# Revit family: 927-00-001-DN80-800
name_source: partatom
category: Pipe Accessories
units: mm (PartAtom-declared; Revit-internal decimal feet)

## family parameters
Always vertical = Yes
Cut with Voids When Loaded = No
Part Type = Valve - Breaks Into
Round Connector Dimension = Use Diameter
Shared = No
Work Plane-Based = No

## types (21) — shared parameters
DN080_PN 10/16 = 927-080-00-020010200
927-080-00-020010200
927-080-00-020010200
927-080-00-020010200
DN100_PN 10/16 = 927-100-00-020010200
927-100-00-020010200
DN150_PN 10/16 = 927-150-00-020010200
DN200_PN10 = 927-200-00-010010200
DN200_PN16 = 927-200-00-020010200
DN250_PN10 = 927-250-00-010010200
DN250_PN16 = 927-250-00-020010200
DN300_PN10 = 927-300-00-010010200
DN300_PN16 = 927-300-00-020010200
DN350_PN10 = 927-350-00-010010200
DN350_PN16 = 927-350-00-020010200
DN400_PN10 = 927-400-00-010010200
DN400_PN16 = 927-400-00-020010200
DN500_PN10 = 927-500-00-010010200
DN500_PN16 = 927-500-00-020010200
DN600_PN10 = 927-600-00-010010200
DN600_PN16 = 927-600-00-020010200
DN700_PN10 = 927-700-00-010010200
DN700_PN16 = 927-700-00-020010200
DN800_PN10 = 927-800-00-010010200
DN800_PN16 = 927-800-00-020010200
Search_table = 927-00-001-DN80-800
URL product pages = https://www.avkvalves.com
zero-valued in all types: 0, Default Elevation, Slot_cut

## per-type parameters (varying)
- DN080_PN 10/16: A=121 mm; B=80 mm; Body_Blend_dim=46 mm; Body_Blend_dim2=80 mm; Body_FL_T=19 mm  [stored 0.062336 ft]; Body_T=6 mm  [stored 0.019685 ft]; Body_arc1=19 mm  [stored 0.062336 ft]; Body_arc_R=180 mm; Body_blend_dim1=72 mm; Body_blend_dim2=80 mm; Body_blend_dim3=80 mm; Body_blend_dim4=60 mm; Body_dim=32 mm  [stored 0.104987 ft]; Body_dim1=48 mm; Body_dim2=56 mm; Body_dim3=22 mm  [stored 0.0721785 ft]; Bolt_dis_H=19 mm  [stored 0.062336 ft]; Bolt_dis_Side=10 mm  [stored 0.0328084 ft]; Bolt_dis_V=23 mm  [stored 0.0754593 ft]; Bolt_location1=20 mm  [stored 0.0656168 ft]; Bolt_location2=20 mm  [stored 0.0656168 ft]; Bolt_location3=54 mm; Bonnet_FL_H1=70 mm; Bonnet_FL_T=19 mm  [stored 0.062336 ft]; Bonnet_FL_dim1=35 mm  [stored 0.114829 ft]; Bonnet_R=20 mm  [stored 0.0656168 ft]; Bonnet_Top_dis=23 mm  [stored 0.0754593 ft]; Bonnet_W=42 mm  [stored 0.137795 ft]; Bonnet_dim=85 mm; Bonnet_dim1=100 mm; Bonnet_dim2=80 mm; Bonnet_dim3=90 mm; Bonnet_sphere_d1=11 mm  [stored 0.0360892 ft]; Bonnet_sphere_d2=60 mm; Bore_R=40 mm  [stored 0.131234 ft]; C=200 mm; D=125 mm; DN=80 mm; Description_=AVK SWING CHECK VALVE, FLANGED; FL_T=16 mm  [stored 0.0524934 ft]; Slot=29 mm  [stored 0.0951444 ft]; Slot_dim1=29 mm  [stored 0.0951444 ft]; Slot_dim2=56 mm; Top_dis_ref=71 mm; Top_rectangle_B=18 mm  [stored 0.0590551 ft]; Top_rectangle_L=42 mm  [stored 0.137795 ft]; rectangle_location=54 mm; top_slot_dis=0 mm  [stored 0 ft]
- DN100_PN 10/16: A=146 mm; B=100 mm; Body_Blend_dim=56 mm; Body_Blend_dim2=100 mm; Body_FL_T=22 mm  [stored 0.0721785 ft]; Body_T=6 mm  [stored 0.019685 ft]; Body_arc1=26 mm; Body_arc_R=230 mm; Body_blend_dim1=88 mm; Body_blend_dim2=96 mm; Body_blend_dim3=88 mm; Body_blend_dim4=66 mm; Body_dim=44 mm  [stored 0.144357 ft]; Body_dim1=58 mm; Body_dim2=72 mm; Body_dim3=31 mm  [stored 0.101706 ft]; Bolt_dis_H=22 mm  [stored 0.0721785 ft]; Bolt_dis_Side=11 mm  [stored 0.0360892 ft]; Bolt_dis_V=26 mm; Bolt_location1=19 mm  [stored 0.062336 ft]; Bolt_location2=22 mm  [stored 0.0721785 ft]; Bolt_location3=65 mm; Bonnet_FL_H1=77 mm; Bonnet_FL_T=26 mm; Bonnet_FL_dim1=30 mm  [stored 0.0984252 ft]; Bonnet_R=20 mm  [stored 0.0656168 ft]; Bonnet_Top_dis=29 mm  [stored 0.0951444 ft]; Bonnet_W=51 mm; Bonnet_dim=100 mm; Bonnet_dim1=110 mm; Bonnet_dim2=88 mm; Bonnet_dim3=105 mm; Bonnet_sphere_d1=13 mm  [stored 0.0426509 ft]; Bonnet_sphere_d2=72 mm; Bore_R=50 mm; C=220 mm; D=140 mm; DN=100 mm; Description_=AVK SWING CHECK VALVE, FLANGED; FL_T=22 mm  [stored 0.0721785 ft]; Slot=35 mm  [stored 0.114829 ft]; Slot_dim1=33 mm  [stored 0.108268 ft]; Slot_dim2=72 mm; Top_dis_ref=86 mm; Top_rectangle_B=22 mm  [stored 0.0721785 ft]; Top_rectangle_L=51 mm; rectangle_location=65 mm; top_slot_dis=0 mm  [stored 0 ft]
- DN150_PN 10/16: A=178 mm; B=150 mm; Body_Blend_dim=81 mm; Body_Blend_dim2=150 mm; Body_FL_T=25 mm  [stored 0.082021 ft]; Body_T=6 mm  [stored 0.019685 ft]; Body_arc1=30 mm  [stored 0.0984252 ft]; Body_arc_R=280 mm; Body_blend_dim1=107 mm; Body_blend_dim2=117 mm; Body_blend_dim3=114 mm; Body_blend_dim4=86 mm; Body_dim=50 mm; Body_dim1=71 mm; Body_dim2=100 mm; Body_dim3=35 mm  [stored 0.114829 ft]; Bolt_dis_H=25 mm  [stored 0.082021 ft]; Bolt_dis_Side=13 mm  [stored 0.0426509 ft]; Bolt_dis_V=30 mm  [stored 0.0984252 ft]; Bolt_location1=27 mm  [stored 0.0885827 ft]; Bolt_location2=28 mm  [stored 0.0918635 ft]; Bolt_location3=79 mm; Bonnet_FL_H1=100 mm; Bonnet_FL_T=30 mm  [stored 0.0984252 ft]; Bonnet_FL_dim1=34 mm  [stored 0.111549 ft]; Bonnet_R=15 mm  [stored 0.0492126 ft]; Bonnet_Top_dis=35 mm  [stored 0.114829 ft]; Bonnet_W=62 mm; Bonnet_dim=125 mm; Bonnet_dim1=143 mm; Bonnet_dim2=114 mm; Bonnet_dim3=130 mm; Bonnet_sphere_d1=15 mm  [stored 0.0492126 ft]; Bonnet_sphere_d2=88 mm; Bore_R=75 mm; C=285 mm; D=175 mm; DN=150 mm; Description_=AVK SWING CHECK VALVE, FLANGED; FL_T=25 mm  [stored 0.082021 ft]; Slot=43 mm  [stored 0.141076 ft]; Slot_dim1=38 mm; Slot_dim2=100 mm; Top_dis_ref=105 mm; Top_rectangle_B=26 mm; Top_rectangle_L=62 mm; rectangle_location=79 mm; top_slot_dis=0 mm  [stored 0 ft]
- DN200_PN10: A=248 mm; B=200 mm; Body_Blend_dim=106 mm; Body_Blend_dim2=200 mm; Body_FL_T=27 mm  [stored 0.0885827 ft]; Body_T=6 mm  [stored 0.019685 ft]; Body_arc1=34 mm  [stored 0.111549 ft]; Body_arc_R=430 mm; Body_blend_dim1=149 mm; Body_blend_dim2=163 mm; Body_blend_dim3=136 mm; Body_blend_dim4=102 mm; Body_dim=56 mm; Body_dim1=99 mm; Body_dim2=128 mm; Body_dim3=39 mm  [stored 0.127953 ft]; Bolt_dis_H=27 mm  [stored 0.0885827 ft]; Bolt_dis_Side=14 mm  [stored 0.0459318 ft]; Bolt_dis_V=32 mm  [stored 0.104987 ft]; Bolt_location1=24 mm  [stored 0.0787402 ft]; Bolt_location2=35 mm  [stored 0.114829 ft]; Bolt_location3=110 mm; Bonnet_FL_H1=119 mm; Bonnet_FL_T=34 mm  [stored 0.111549 ft]; Bonnet_FL_dim1=34 mm  [stored 0.111549 ft]; Bonnet_R=18 mm  [stored 0.0590551 ft]; Bonnet_Top_dis=54 mm; Bonnet_W=87 mm; Bonnet_dim=170 mm; Bonnet_dim1=170 mm; Bonnet_dim2=136 mm; Bonnet_dim3=175 mm; Bonnet_sphere_d1=16 mm  [stored 0.0524934 ft]; Bonnet_sphere_d2=123 mm; Bore_R=100 mm; C=340 mm; D=215 mm; DN=200 mm; Description_=AVK SWING CHECK VALVE, FLANGED; FL_T=28 mm  [stored 0.0918635 ft]; Slot=60 mm; Slot_dim1=41 mm  [stored 0.134514 ft]; Slot_dim2=128 mm; Top_dis_ref=146 mm; Top_rectangle_B=37 mm  [stored 0.121391 ft]; Top_rectangle_L=86 mm; rectangle_location=110 mm; top_slot_dis=0 mm  [stored 0 ft]
- DN200_PN16: A=248 mm; B=200 mm; Body_Blend_dim=106 mm; Body_Blend_dim2=200 mm; Body_FL_T=27 mm  [stored 0.0885827 ft]; Body_T=6 mm  [stored 0.019685 ft]; Body_arc1=34 mm  [stored 0.111549 ft]; Body_arc_R=430 mm; Body_blend_dim1=149 mm; Body_blend_dim2=163 mm; Body_blend_dim3=136 mm; Body_blend_dim4=102 mm; Body_dim=56 mm; Body_dim1=99 mm; Body_dim2=128 mm; Body_dim3=39 mm  [stored 0.127953 ft]; Bolt_dis_H=27 mm  [stored 0.0885827 ft]; Bolt_dis_Side=14 mm  [stored 0.0459318 ft]; Bolt_dis_V=32 mm  [stored 0.104987 ft]; Bolt_location1=24 mm  [stored 0.0787402 ft]; Bolt_location2=35 mm  [stored 0.114829 ft]; Bolt_location3=110 mm; Bonnet_FL_H1=119 mm; Bonnet_FL_T=34 mm  [stored 0.111549 ft]; Bonnet_FL_dim1=34 mm  [stored 0.111549 ft]; Bonnet_R=21 mm  [stored 0.0688976 ft]; Bonnet_Top_dis=54 mm; Bonnet_W=87 mm; Bonnet_dim=170 mm; Bonnet_dim1=170 mm; Bonnet_dim2=136 mm; Bonnet_dim3=175 mm; Bonnet_sphere_d1=16 mm  [stored 0.0524934 ft]; Bonnet_sphere_d2=123 mm; Bore_R=100 mm; C=340 mm; D=215 mm; DN=200 mm; Description_=AVK SWING CHECK VALVE, FLANGED; FL_T=28 mm  [stored 0.0918635 ft]; Slot=60 mm; Slot_dim1=41 mm  [stored 0.134514 ft]; Slot_dim2=128 mm; Top_dis_ref=146 mm; Top_rectangle_B=37 mm  [stored 0.121391 ft]; Top_rectangle_L=86 mm; rectangle_location=110 mm; top_slot_dis=0 mm  [stored 0 ft]
- DN250_PN10: A=311 mm; B=250 mm; Body_Blend_dim=132 mm; Body_Blend_dim2=250 mm; Body_FL_T=31 mm  [stored 0.101706 ft]; Body_T=7 mm  [stored 0.0229659 ft]; Body_arc1=35 mm  [stored 0.114829 ft]; Body_arc_R=545 mm; Body_blend_dim1=187 mm; Body_blend_dim2=205 mm; Body_blend_dim3=160 mm; Body_blend_dim4=120 mm; Body_dim=58 mm; Body_dim1=124 mm; Body_dim2=154 mm; Body_dim3=41 mm  [stored 0.134514 ft]; Bolt_dis_H=31 mm  [stored 0.101706 ft]; Bolt_dis_Side=16 mm  [stored 0.0524934 ft]; Bolt_dis_V=37 mm  [stored 0.121391 ft]; Bolt_location1=23 mm  [stored 0.0754593 ft]; Bolt_location2=54 mm; Bolt_location3=139 mm; Bonnet_FL_H1=140 mm; Bonnet_FL_T=35 mm  [stored 0.114829 ft]; Bonnet_FL_dim1=37 mm  [stored 0.121391 ft]; Bonnet_R=24 mm  [stored 0.0787402 ft]; Bonnet_Top_dis=68 mm; Bonnet_W=109 mm; Bonnet_dim=230 mm; Bonnet_dim1=200 mm; Bonnet_dim2=160 mm; Bonnet_dim3=235 mm; Bonnet_sphere_d1=18 mm  [stored 0.0590551 ft]; Bonnet_sphere_d2=154 mm; Bore_R=125 mm; C=400 mm; D=280 mm; DN=250 mm; Description_=AVK SWING CHECK VALVE, FLANGED; FL_T=29 mm  [stored 0.0951444 ft]; Slot=75 mm; Slot_dim1=47 mm; Slot_dim2=154 mm; Top_dis_ref=183 mm; Top_rectangle_B=46 mm; Top_rectangle_L=108 mm; rectangle_location=139 mm; top_slot_dis=0 mm  [stored 0 ft]
- DN250_PN16: A=311 mm; B=250 mm; Body_Blend_dim=132 mm; Body_Blend_dim2=250 mm; Body_FL_T=31 mm  [stored 0.101706 ft]; Body_T=7 mm  [stored 0.0229659 ft]; Body_arc1=35 mm  [stored 0.114829 ft]; Body_arc_R=545 mm; Body_blend_dim1=187 mm; Body_blend_dim2=205 mm; Body_blend_dim3=160 mm; Body_blend_dim4=120 mm; Body_dim=58 mm; Body_dim1=124 mm; Body_dim2=154 mm; Body_dim3=41 mm  [stored 0.134514 ft]; Bolt_dis_H=31 mm  [stored 0.101706 ft]; Bolt_dis_Side=16 mm  [stored 0.0524934 ft]; Bolt_dis_V=37 mm  [stored 0.121391 ft]; Bolt_location1=23 mm  [stored 0.0754593 ft]; Bolt_location2=54 mm; Bolt_location3=139 mm; Bonnet_FL_H1=140 mm; Bonnet_FL_T=35 mm  [stored 0.114829 ft]; Bonnet_FL_dim1=37 mm  [stored 0.121391 ft]; Bonnet_R=24 mm  [stored 0.0787402 ft]; Bonnet_Top_dis=68 mm; Bonnet_W=109 mm; Bonnet_dim=230 mm; Bonnet_dim1=200 mm; Bonnet_dim2=160 mm; Bonnet_dim3=235 mm; Bonnet_sphere_d1=18 mm  [stored 0.0590551 ft]; Bonnet_sphere_d2=154 mm; Bore_R=125 mm; C=400 mm; D=280 mm; DN=250 mm; Description_=AVK SWING CHECK VALVE, FLANGED; FL_T=29 mm  [stored 0.0951444 ft]; Slot=75 mm; Slot_dim1=47 mm; Slot_dim2=154 mm; Top_dis_ref=183 mm; Top_rectangle_B=46 mm; Top_rectangle_L=108 mm; rectangle_location=139 mm; top_slot_dis=0 mm  [stored 0 ft]
- DN300_PN10: A=349 mm; B=300 mm; Body_Blend_dim=157 mm; Body_Blend_dim2=300 mm; Body_FL_T=34 mm  [stored 0.111549 ft]; Body_T=7 mm  [stored 0.0229659 ft]; Body_arc1=37 mm  [stored 0.121391 ft]; Body_arc_R=590 mm; Body_blend_dim1=209 mm; Body_blend_dim2=230 mm; Body_blend_dim3=182 mm; Body_blend_dim4=137 mm; Body_dim=62 mm; Body_dim1=140 mm; Body_dim2=181 mm; Body_dim3=43 mm  [stored 0.141076 ft]; Bolt_dis_H=34 mm  [stored 0.111549 ft]; Bolt_dis_Side=17 mm; Bolt_dis_V=41 mm  [stored 0.134514 ft]; Bolt_location1=27 mm  [stored 0.0885827 ft]; Bolt_location2=55 mm; Bolt_location3=155 mm; Bonnet_FL_H1=159 mm; Bonnet_FL_T=37 mm  [stored 0.121391 ft]; Bonnet_FL_dim1=37 mm  [stored 0.121391 ft]; Bonnet_R=27 mm  [stored 0.0885827 ft]; Bonnet_Top_dis=74 mm; Bonnet_W=122 mm; Bonnet_dim=250 mm; Bonnet_dim1=228 mm; Bonnet_dim2=182 mm; Bonnet_dim3=255 mm; Bonnet_sphere_d1=20 mm  [stored 0.0656168 ft]; Bonnet_sphere_d2=173 mm; Bore_R=150 mm; C=455 mm; D=300 mm; DN=300 mm; Description_=AVK SWING CHECK VALVE, FLANGED; FL_T=31 mm  [stored 0.101706 ft]; Slot=85 mm; Slot_dim1=51 mm; Slot_dim2=181 mm; Top_dis_ref=206 mm; Top_rectangle_B=52 mm; Top_rectangle_L=121 mm; rectangle_location=155 mm; top_slot_dis=0 mm  [stored 0 ft]
- DN300_PN16: A=349 mm; B=300 mm; Body_Blend_dim=157 mm; Body_Blend_dim2=300 mm; Body_FL_T=34 mm  [stored 0.111549 ft]; Body_T=7 mm  [stored 0.0229659 ft]; Body_arc1=37 mm  [stored 0.121391 ft]; Body_arc_R=590 mm; Body_blend_dim1=209 mm; Body_blend_dim2=230 mm; Body_blend_dim3=182 mm; Body_blend_dim4=137 mm; Body_dim=62 mm; Body_dim1=140 mm; Body_dim2=181 mm; Body_dim3=43 mm  [stored 0.141076 ft]; Bolt_dis_H=34 mm  [stored 0.111549 ft]; Bolt_dis_Side=17 mm; Bolt_dis_V=41 mm  [stored 0.134514 ft]; Bolt_location1=27 mm  [stored 0.0885827 ft]; Bolt_location2=55 mm; Bolt_location3=155 mm; Bonnet_FL_H1=159 mm; Bonnet_FL_T=37 mm  [stored 0.121391 ft]; Bonnet_FL_dim1=37 mm  [stored 0.121391 ft]; Bonnet_R=27 mm  [stored 0.0885827 ft]; Bonnet_Top_dis=74 mm; Bonnet_W=122 mm; Bonnet_dim=250 mm; Bonnet_dim1=228 mm; Bonnet_dim2=182 mm; Bonnet_dim3=255 mm; Bonnet_sphere_d1=20 mm  [stored 0.0656168 ft]; Bonnet_sphere_d2=173 mm; Bore_R=150 mm; C=455 mm; D=300 mm; DN=300 mm; Description_=AVK SWING CHECK VALVE, FLANGED; FL_T=31 mm  [stored 0.101706 ft]; Slot=85 mm; Slot_dim1=51 mm; Slot_dim2=181 mm; Top_dis_ref=206 mm; Top_rectangle_B=52 mm; Top_rectangle_L=121 mm; rectangle_location=155 mm; top_slot_dis=0 mm  [stored 0 ft]
- DN350_PN10: A=394 mm; B=350 mm; Body_Blend_dim=183 mm; Body_Blend_dim2=350 mm; Body_FL_T=37 mm  [stored 0.121391 ft]; Body_T=8 mm  [stored 0.0262467 ft]; Body_arc1=40 mm  [stored 0.131234 ft]; Body_arc_R=670 mm; Body_blend_dim1=236 mm; Body_blend_dim2=260 mm; Body_blend_dim3=202 mm; Body_blend_dim4=152 mm; Body_dim=66 mm; Body_dim1=157 mm; Body_dim2=208 mm; Body_dim3=46 mm; Bolt_dis_H=37 mm  [stored 0.121391 ft]; Bolt_dis_Side=19 mm  [stored 0.062336 ft]; Bolt_dis_V=44 mm  [stored 0.144357 ft]; Bolt_location1=29 mm  [stored 0.0951444 ft]; Bolt_location2=73 mm; Bolt_location3=175 mm; Bonnet_FL_H1=177 mm; Bonnet_FL_T=40 mm  [stored 0.131234 ft]; Bonnet_FL_dim1=36 mm  [stored 0.11811 ft]; Bonnet_R=30 mm  [stored 0.0984252 ft]; Bonnet_Top_dis=84 mm; Bonnet_W=138 mm; Bonnet_dim=300 mm; Bonnet_dim1=253 mm; Bonnet_dim2=202 mm; Bonnet_dim3=305 mm; Bonnet_sphere_d1=22 mm  [stored 0.0721785 ft]; Bonnet_sphere_d2=195 mm; Bore_R=175 mm; C=505 mm; D=315 mm; DN=350 mm; Description_=AVK SWING CHECK VALVE, FLANGED; FL_T=33 mm  [stored 0.108268 ft]; Slot=95 mm; Slot_dim1=56 mm; Slot_dim2=208 mm; Top_dis_ref=232 mm; Top_rectangle_B=58 mm; Top_rectangle_L=136 mm; rectangle_location=175 mm; top_slot_dis=0 mm  [stored 0 ft]
- DN350_PN16: A=394 mm; B=350 mm; Body_Blend_dim=183 mm; Body_Blend_dim2=350 mm; Body_FL_T=37 mm  [stored 0.121391 ft]; Body_T=8 mm  [stored 0.0262467 ft]; Body_arc1=40 mm  [stored 0.131234 ft]; Body_arc_R=670 mm; Body_blend_dim1=236 mm; Body_blend_dim2=260 mm; Body_blend_dim3=202 mm; Body_blend_dim4=152 mm; Body_dim=66 mm; Body_dim1=157 mm; Body_dim2=208 mm; Body_dim3=46 mm; Bolt_dis_H=37 mm  [stored 0.121391 ft]; Bolt_dis_Side=19 mm  [stored 0.062336 ft]; Bolt_dis_V=44 mm  [stored 0.144357 ft]; Bolt_location1=29 mm  [stored 0.0951444 ft]; Bolt_location2=73 mm; Bolt_location3=175 mm; Bonnet_FL_H1=177 mm; Bonnet_FL_T=40 mm  [stored 0.131234 ft]; Bonnet_FL_dim1=36 mm  [stored 0.11811 ft]; Bonnet_R=30 mm  [stored 0.0984252 ft]; Bonnet_Top_dis=84 mm; Bonnet_W=138 mm; Bonnet_dim=300 mm; Bonnet_dim1=253 mm; Bonnet_dim2=202 mm; Bonnet_dim3=305 mm; Bonnet_sphere_d1=22 mm  [stored 0.0721785 ft]; Bonnet_sphere_d2=195 mm; Bore_R=175 mm; C=505 mm; D=315 mm; DN=350 mm; Description_=AVK SWING CHECK VALVE, FLANGED; FL_T=33 mm  [stored 0.108268 ft]; Slot=95 mm; Slot_dim1=56 mm; Slot_dim2=208 mm; Top_dis_ref=232 mm; Top_rectangle_B=58 mm; Top_rectangle_L=136 mm; rectangle_location=175 mm; top_slot_dis=0 mm  [stored 0 ft]
- DN400_PN10: A=457 mm; B=400 mm; Body_Blend_dim=208 mm; Body_Blend_dim2=400 mm; Body_FL_T=39 mm  [stored 0.127953 ft]; Body_T=8 mm  [stored 0.0262467 ft]; Body_arc1=42 mm  [stored 0.137795 ft]; Body_arc_R=770 mm; Body_blend_dim1=274 mm; Body_blend_dim2=302 mm; Body_blend_dim3=232 mm; Body_blend_dim4=174 mm; Body_dim=70 mm; Body_dim1=183 mm; Body_dim2=235 mm; Body_dim3=49 mm; Bolt_dis_H=39 mm  [stored 0.127953 ft]; Bolt_dis_Side=20 mm  [stored 0.0656168 ft]; Bolt_dis_V=47 mm; Bolt_location1=32 mm  [stored 0.104987 ft]; Bolt_location2=79 mm; Bolt_location3=204 mm; Bonnet_FL_H1=203 mm; Bonnet_FL_T=42 mm  [stored 0.137795 ft]; Bonnet_FL_dim1=44 mm  [stored 0.144357 ft]; Bonnet_R=33 mm  [stored 0.108268 ft]; Bonnet_Top_dis=96 mm; Bonnet_W=160 mm; Bonnet_dim=340 mm; Bonnet_dim1=290 mm; Bonnet_dim2=232 mm; Bonnet_dim3=345 mm; Bonnet_sphere_d1=23 mm  [stored 0.0754593 ft]; Bonnet_sphere_d2=226 mm; Bore_R=200 mm; C=580 mm; D=355 mm; DN=400 mm; Description_=AVK SWING CHECK VALVE, FLANGED; FL_T=35 mm  [stored 0.114829 ft]; Slot=111 mm; Slot_dim1=59 mm; Slot_dim2=235 mm; Top_dis_ref=269 mm; Top_rectangle_B=68 mm; Top_rectangle_L=158 mm; rectangle_location=204 mm; top_slot_dis=0 mm  [stored 0 ft]
- DN400_PN16: A=457 mm; B=400 mm; Body_Blend_dim=208 mm; Body_Blend_dim2=400 mm; Body_FL_T=39 mm  [stored 0.127953 ft]; Body_T=8 mm  [stored 0.0262467 ft]; Body_arc1=42 mm  [stored 0.137795 ft]; Body_arc_R=770 mm; Body_blend_dim1=274 mm; Body_blend_dim2=302 mm; Body_blend_dim3=232 mm; Body_blend_dim4=174 mm; Body_dim=70 mm; Body_dim1=183 mm; Body_dim2=235 mm; Body_dim3=49 mm; Bolt_dis_H=39 mm  [stored 0.127953 ft]; Bolt_dis_Side=20 mm  [stored 0.0656168 ft]; Bolt_dis_V=47 mm; Bolt_location1=32 mm  [stored 0.104987 ft]; Bolt_location2=79 mm; Bolt_location3=204 mm; Bonnet_FL_H1=203 mm; Bonnet_FL_T=42 mm  [stored 0.137795 ft]; Bonnet_FL_dim1=44 mm  [stored 0.144357 ft]; Bonnet_R=33 mm  [stored 0.108268 ft]; Bonnet_Top_dis=96 mm; Bonnet_W=160 mm; Bonnet_dim=340 mm; Bonnet_dim1=290 mm; Bonnet_dim2=232 mm; Bonnet_dim3=345 mm; Bonnet_sphere_d1=23 mm  [stored 0.0754593 ft]; Bonnet_sphere_d2=226 mm; Bore_R=200 mm; C=580 mm; D=355 mm; DN=400 mm; Description_=AVK SWING CHECK VALVE, FLANGED; FL_T=35 mm  [stored 0.114829 ft]; Slot=111 mm; Slot_dim1=59 mm; Slot_dim2=235 mm; Top_dis_ref=269 mm; Top_rectangle_B=68 mm; Top_rectangle_L=158 mm; rectangle_location=204 mm; top_slot_dis=0 mm  [stored 0 ft]
- DN500_PN10: A=508 mm; B=500 mm; Body_Blend_dim=259 mm; Body_Blend_dim2=500 mm; Body_FL_T=43 mm  [stored 0.141076 ft]; Body_T=9 mm  [stored 0.0295276 ft]; Body_arc1=44 mm  [stored 0.144357 ft]; Body_arc_R=890 mm; Body_blend_dim1=305 mm; Body_blend_dim2=335 mm; Body_blend_dim3=279 mm; Body_blend_dim4=209 mm; Body_dim=74 mm; Body_dim1=203 mm; Body_dim2=287 mm; Body_dim3=52 mm; Bolt_dis_H=43 mm  [stored 0.141076 ft]; Bolt_dis_Side=22 mm  [stored 0.0721785 ft]; Bolt_dis_V=52 mm; Bolt_location1=49 mm; Bolt_location2=109 mm; Bolt_location3=226 mm; Bonnet_FL_H1=244 mm; Bonnet_FL_T=44 mm  [stored 0.144357 ft]; Bonnet_FL_dim1=50 mm; Bonnet_R=36 mm  [stored 0.11811 ft]; Bonnet_Top_dis=111 mm; Bonnet_W=178 mm; Bonnet_dim=410 mm; Bonnet_dim1=349 mm; Bonnet_dim2=279 mm; Bonnet_dim3=415 mm; Bonnet_sphere_d1=25 mm  [stored 0.082021 ft]; Bonnet_sphere_d2=251 mm; Bore_R=250 mm; C=698 mm; D=430 mm; DN=500 mm; Description_=AVK SWING CHECK VALVE, FLANGED; FL_T=37 mm  [stored 0.121391 ft]; Slot=123 mm; Slot_dim1=65 mm; Slot_dim2=287 mm; Top_dis_ref=299 mm; Top_rectangle_B=75 mm; Top_rectangle_L=176 mm; rectangle_location=226 mm; top_slot_dis=0 mm  [stored 0 ft]
- DN500_PN16: A=508 mm; B=500 mm; Body_Blend_dim=259 mm; Body_Blend_dim2=500 mm; Body_FL_T=43 mm  [stored 0.141076 ft]; Body_T=9 mm  [stored 0.0295276 ft]; Body_arc1=44 mm  [stored 0.144357 ft]; Body_arc_R=890 mm; Body_blend_dim1=305 mm; Body_blend_dim2=335 mm; Body_blend_dim3=279 mm; Body_blend_dim4=209 mm; Body_dim=74 mm; Body_dim1=203 mm; Body_dim2=287 mm; Body_dim3=52 mm; Bolt_dis_H=43 mm  [stored 0.141076 ft]; Bolt_dis_Side=22 mm  [stored 0.0721785 ft]; Bolt_dis_V=52 mm; Bolt_location1=49 mm; Bolt_location2=109 mm; Bolt_location3=226 mm; Bonnet_FL_H1=244 mm; Bonnet_FL_T=44 mm  [stored 0.144357 ft]; Bonnet_FL_dim1=50 mm; Bonnet_R=36 mm  [stored 0.11811 ft]; Bonnet_Top_dis=111 mm; Bonnet_W=178 mm; Bonnet_dim=410 mm; Bonnet_dim1=349 mm; Bonnet_dim2=279 mm; Bonnet_dim3=415 mm; Bonnet_sphere_d1=25 mm  [stored 0.082021 ft]; Bonnet_sphere_d2=251 mm; Bore_R=250 mm; C=698 mm; D=430 mm; DN=500 mm; Description_=AVK SWING CHECK VALVE, FLANGED; FL_T=37 mm  [stored 0.121391 ft]; Slot=123 mm; Slot_dim1=65 mm; Slot_dim2=287 mm; Top_dis_ref=299 mm; Top_rectangle_B=75 mm; Top_rectangle_L=176 mm; rectangle_location=226 mm; top_slot_dis=0 mm  [stored 0 ft]
- DN600_PN10: A=610 mm; B=600 mm; Body_Blend_dim=309 mm; Body_Blend_dim2=600 mm; Body_FL_T=46 mm; Body_T=9 mm  [stored 0.0295276 ft]; Body_arc1=47 mm; Body_arc_R=1000 mm; Body_blend_dim1=366 mm; Body_blend_dim2=402 mm; Body_blend_dim3=312 mm; Body_blend_dim4=234 mm; Body_dim=78 mm; Body_dim1=244 mm; Body_dim2=339 mm; Body_dim3=55 mm; Bolt_dis_H=46 mm; Bolt_dis_Side=23 mm  [stored 0.0754593 ft]; Bolt_dis_V=55 mm; Bolt_location1=44 mm  [stored 0.144357 ft]; Bolt_location2=116 mm; Bolt_location3=272 mm; Bonnet_FL_H1=273 mm; Bonnet_FL_T=47 mm; Bonnet_FL_dim1=41 mm  [stored 0.134514 ft]; Bonnet_R=39 mm  [stored 0.127953 ft]; Bonnet_Top_dis=125 mm; Bonnet_W=213 mm; Bonnet_dim=470 mm; Bonnet_dim1=390 mm; Bonnet_dim2=312 mm; Bonnet_dim3=475 mm; Bonnet_sphere_d1=27 mm  [stored 0.0885827 ft]; Bonnet_sphere_d2=302 mm; Bore_R=300 mm; C=780 mm; D=495 mm; DN=600 mm; Description_=AVK SWING CHECK VALVE, FLANGED; FL_T=39 mm  [stored 0.127953 ft]; Slot=148 mm; Slot_dim1=69 mm; Slot_dim2=339 mm; Top_dis_ref=359 mm; Top_rectangle_B=91 mm; Top_rectangle_L=211 mm; rectangle_location=272 mm; top_slot_dis=0 mm  [stored 0 ft]
- DN600_PN16: A=610 mm; B=600 mm; Body_Blend_dim=309 mm; Body_Blend_dim2=600 mm; Body_FL_T=46 mm; Body_T=9 mm  [stored 0.0295276 ft]; Body_arc1=47 mm; Body_arc_R=1000 mm; Body_blend_dim1=366 mm; Body_blend_dim2=402 mm; Body_blend_dim3=312 mm; Body_blend_dim4=234 mm; Body_dim=78 mm; Body_dim1=244 mm; Body_dim2=339 mm; Body_dim3=55 mm; Bolt_dis_H=46 mm; Bolt_dis_Side=23 mm  [stored 0.0754593 ft]; Bolt_dis_V=55 mm; Bolt_location1=44 mm  [stored 0.144357 ft]; Bolt_location2=116 mm; Bolt_location3=272 mm; Bonnet_FL_H1=273 mm; Bonnet_FL_T=47 mm; Bonnet_FL_dim1=41 mm  [stored 0.134514 ft]; Bonnet_R=39 mm  [stored 0.127953 ft]; Bonnet_Top_dis=125 mm; Bonnet_W=213 mm; Bonnet_dim=470 mm; Bonnet_dim1=390 mm; Bonnet_dim2=312 mm; Bonnet_dim3=475 mm; Bonnet_sphere_d1=27 mm  [stored 0.0885827 ft]; Bonnet_sphere_d2=302 mm; Bore_R=300 mm; C=780 mm; D=495 mm; DN=600 mm; Description_=AVK SWING CHECK VALVE, FLANGED; FL_T=39 mm  [stored 0.127953 ft]; Slot=148 mm; Slot_dim1=69 mm; Slot_dim2=339 mm; Top_dis_ref=359 mm; Top_rectangle_B=91 mm; Top_rectangle_L=211 mm; rectangle_location=272 mm; top_slot_dis=0 mm  [stored 0 ft]
- DN700_PN10: A=750 mm; B=700 mm; Body_Blend_dim=360 mm; Body_Blend_dim2=700 mm; Body_FL_T=49 mm; Body_T=10 mm  [stored 0.0328084 ft]; Body_arc1=49 mm; Body_arc_R=1220 mm; Body_blend_dim1=450 mm; Body_blend_dim2=495 mm; Body_blend_dim3=364 mm; Body_blend_dim4=273 mm; Body_dim=82 mm; Body_dim1=300 mm; Body_dim2=391 mm; Body_dim3=57 mm; Bolt_dis_H=49 mm; Bolt_dis_Side=25 mm  [stored 0.082021 ft]; Bolt_dis_V=59 mm; Bolt_location1=42 mm  [stored 0.137795 ft]; Bolt_location2=143 mm; Bolt_location3=334 mm; Bonnet_FL_H1=319 mm; Bonnet_FL_T=49 mm; Bonnet_FL_dim1=51 mm; Bonnet_R=42 mm  [stored 0.137795 ft]; Bonnet_Top_dis=153 mm; Bonnet_W=263 mm; Bonnet_dim=580 mm; Bonnet_dim1=455 mm; Bonnet_dim2=364 mm; Bonnet_dim3=585 mm; Bonnet_sphere_d1=29 mm  [stored 0.0951444 ft]; Bonnet_sphere_d2=371 mm; Bore_R=350 mm; C=910 mm; D=580 mm; DN=700 mm; Description_=AVK SWING CHECK VALVE, FLANGED; FL_T=41 mm  [stored 0.134514 ft]; Slot=182 mm; Slot_dim1=74 mm; Slot_dim2=391 mm; Top_dis_ref=442 mm; Top_rectangle_B=111 mm; Top_rectangle_L=260 mm; rectangle_location=334 mm; top_slot_dis=0 mm  [stored 0 ft]
- DN700_PN16: A=750 mm; B=700 mm; Body_Blend_dim=360 mm; Body_Blend_dim2=700 mm; Body_FL_T=49 mm; Body_T=10 mm  [stored 0.0328084 ft]; Body_arc1=49 mm; Body_arc_R=1220 mm; Body_blend_dim1=450 mm; Body_blend_dim2=495 mm; Body_blend_dim3=364 mm; Body_blend_dim4=273 mm; Body_dim=82 mm; Body_dim1=300 mm; Body_dim2=391 mm; Body_dim3=57 mm; Bolt_dis_H=49 mm; Bolt_dis_Side=25 mm  [stored 0.082021 ft]; Bolt_dis_V=59 mm; Bolt_location1=42 mm  [stored 0.137795 ft]; Bolt_location2=143 mm; Bolt_location3=334 mm; Bonnet_FL_H1=319 mm; Bonnet_FL_T=49 mm; Bonnet_FL_dim1=51 mm; Bonnet_R=42 mm  [stored 0.137795 ft]; Bonnet_Top_dis=153 mm; Bonnet_W=263 mm; Bonnet_dim=580 mm; Bonnet_dim1=455 mm; Bonnet_dim2=364 mm; Bonnet_dim3=585 mm; Bonnet_sphere_d1=29 mm  [stored 0.0951444 ft]; Bonnet_sphere_d2=371 mm; Bore_R=350 mm; C=910 mm; D=580 mm; DN=700 mm; Description_=AVK SWING CHECK VALVE, FLANGED; FL_T=41 mm  [stored 0.134514 ft]; Slot=182 mm; Slot_dim1=74 mm; Slot_dim2=391 mm; Top_dis_ref=442 mm; Top_rectangle_B=111 mm; Top_rectangle_L=260 mm; rectangle_location=334 mm; top_slot_dis=0 mm  [stored 0 ft]
- DN800_PN10: A=850 mm; B=780 mm; Body_Blend_dim=410 mm; Body_Blend_dim2=800 mm; Body_FL_T=51 mm; Body_T=10 mm  [stored 0.0328084 ft]; Body_arc1=52 mm; Body_arc_R=1500 mm; Body_blend_dim1=510 mm; Body_blend_dim2=561 mm; Body_blend_dim3=410 mm; Body_blend_dim4=308 mm; Body_dim=86 mm; Body_dim1=340 mm; Body_dim2=443 mm; Body_dim3=60 mm; Bolt_dis_H=51 mm; Bolt_dis_Side=26 mm; Bolt_dis_V=61 mm; Bolt_location1=46 mm; Bolt_location2=156 mm; Bolt_location3=379 mm; Bonnet_FL_H1=359 mm; Bonnet_FL_T=52 mm; Bonnet_FL_dim1=56 mm; Bonnet_R=45 mm; Bonnet_Top_dis=188 mm; Bonnet_W=298 mm; Bonnet_dim=650 mm; Bonnet_dim1=513 mm; Bonnet_dim2=410 mm; Bonnet_dim3=655 mm; Bonnet_sphere_d1=30 mm  [stored 0.0984252 ft]; Bonnet_sphere_d2=421 mm; Bore_R=400 mm; C=1025 mm; D=600 mm; DN=800 mm; Description_=AVK SWING CHECK VALVE, FLANGED; FL_T=43 mm  [stored 0.141076 ft]; Slot=206 mm; Slot_dim1=77 mm; Slot_dim2=443 mm; Top_dis_ref=501 mm; Top_rectangle_B=126 mm; Top_rectangle_L=295 mm; rectangle_location=379 mm; top_slot_dis=1 mm  [stored 0.00328084 ft]
- DN800_PN16: A=850 mm; B=780 mm; Body_Blend_dim=410 mm; Body_Blend_dim2=800 mm; Body_FL_T=51 mm; Body_T=10 mm  [stored 0.0328084 ft]; Body_arc1=52 mm; Body_arc_R=1500 mm; Body_blend_dim1=510 mm; Body_blend_dim2=561 mm; Body_blend_dim3=410 mm; Body_blend_dim4=308 mm; Body_dim=86 mm; Body_dim1=340 mm; Body_dim2=443 mm; Body_dim3=60 mm; Bolt_dis_H=51 mm; Bolt_dis_Side=26 mm; Bolt_dis_V=61 mm; Bolt_location1=46 mm; Bolt_location2=156 mm; Bolt_location3=379 mm; Bonnet_FL_H1=359 mm; Bonnet_FL_T=52 mm; Bonnet_FL_dim1=56 mm; Bonnet_R=45 mm; Bonnet_Top_dis=188 mm; Bonnet_W=298 mm; Bonnet_dim=650 mm; Bonnet_dim1=513 mm; Bonnet_dim2=410 mm; Bonnet_dim3=655 mm; Bonnet_sphere_d1=30 mm  [stored 0.0984252 ft]; Bonnet_sphere_d2=421 mm; Bore_R=400 mm; C=1025 mm; D=600 mm; DN=800 mm; Description_=AVK SWING CHECK VALVE, FLANGED, PN10/16; FL_T=43 mm  [stored 0.141076 ft]; Slot=206 mm; Slot_dim1=77 mm; Slot_dim2=443 mm; Top_dis_ref=501 mm; Top_rectangle_B=126 mm; Top_rectangle_L=295 mm; rectangle_location=379 mm; top_slot_dis=1 mm  [stored 0.00328084 ft]

note: [stored X ft] marks values corroborated as IEEE doubles in the binary element streams (Revit-internal decimal feet)

## geometry (parser evidence)
native form markers: Sweep x7
no freeform markers — native parametric forms only
